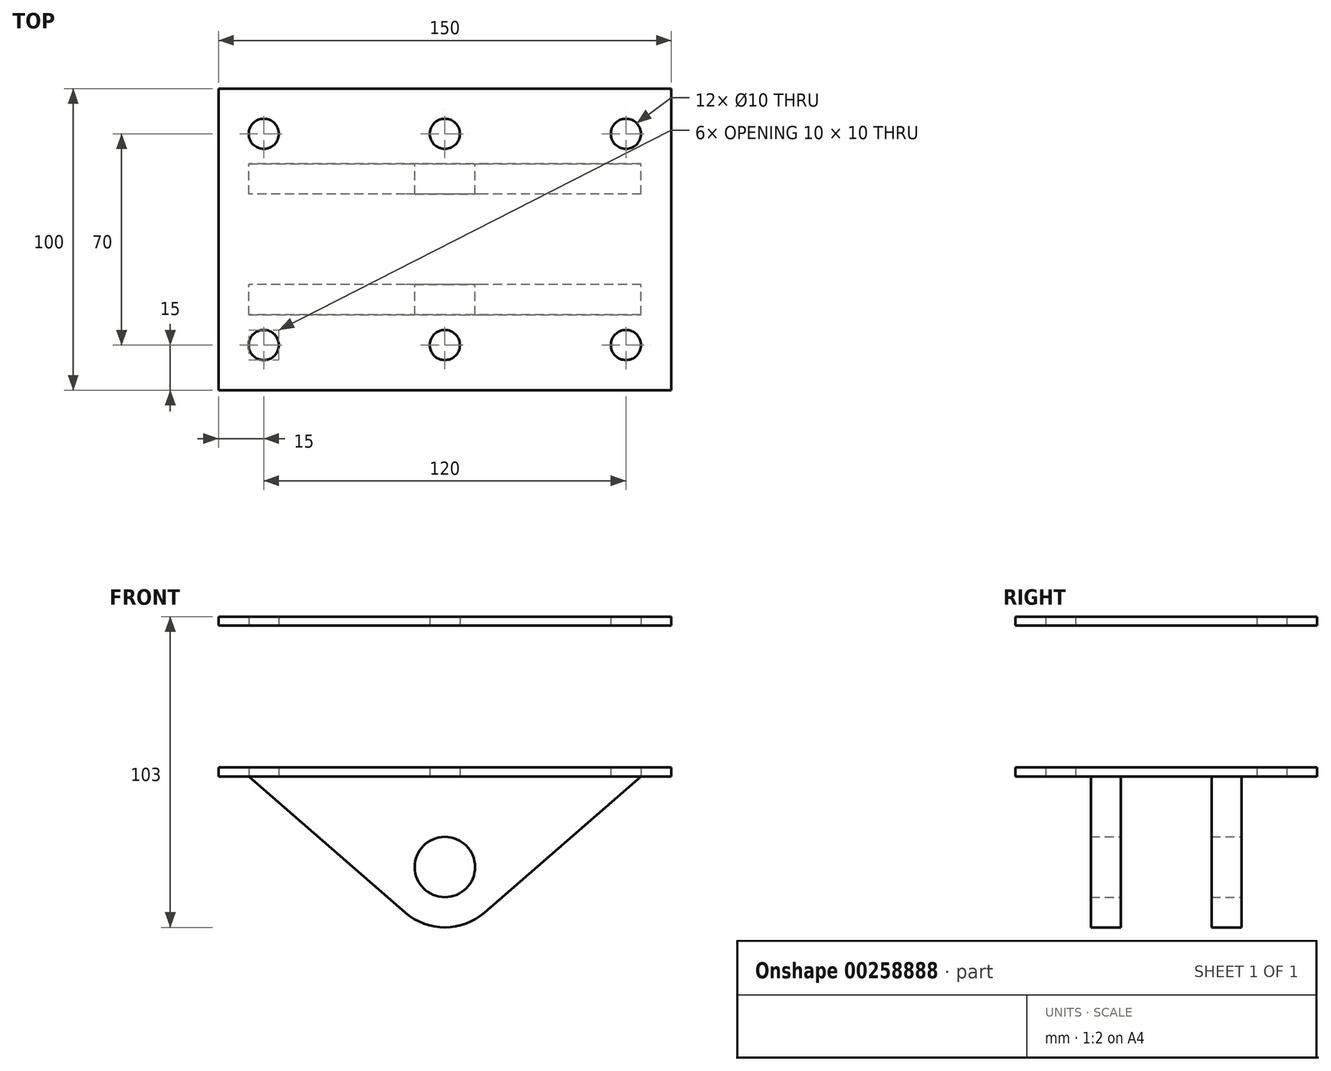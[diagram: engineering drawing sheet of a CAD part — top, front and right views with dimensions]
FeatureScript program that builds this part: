
annotation { "Feature Type Name" : "Feature", "Feature Type Description" : "" }
export const myFeature = defineFeature(function(context is Context, id is Id, definition is map)
    precondition{}
    {
        {
            var Q0;
            Q0=qCreatedBy(makeId("Top.planeOp"),FACE);
            var sketch = newSketch(context, id + "F0", { "sketchPlane" : qUnion([Q0])});
            skLineSegment(sketch, "E0.bottom", {"start": v(-75, 50) * mm, "end": v(75, 50) * mm});
            skLineSegment(sketch, "E0.top", {"start": v(-75, -50) * mm, "end": v(75, -50) * mm});
            skLineSegment(sketch, "E0.left", {"start": v(-75, 50) * mm, "end": v(-75, -50) * mm});
            skLineSegment(sketch, "E0.right", {"start": v(75, 50) * mm, "end": v(75, -50) * mm});
            skPoint(sketch, "E0.middle", {"position": v(0, 0) * mm});
            skLineSegment(sketch, "E1.bottom", {"start": v(-60, 35) * mm, "end": v(60, 35) * mm, "construction": true});
            skLineSegment(sketch, "E1.top", {"start": v(-60, -35) * mm, "end": v(60, -35) * mm, "construction": true});
            skLineSegment(sketch, "E1.left", {"start": v(-60, 35) * mm, "end": v(-60, -35) * mm, "construction": true});
            skLineSegment(sketch, "E1.right", {"start": v(60, 35) * mm, "end": v(60, -35) * mm, "construction": true});
            skCircle(sketch, "E2", {"center": v(-60, 35) * mm, "radius": 5 * mm});
            skCircle(sketch, "E3", {"center": v(-60, -35) * mm, "radius": 5 * mm});
            skCircle(sketch, "E4", {"center": v(60, -35) * mm, "radius": 5 * mm});
            skCircle(sketch, "E5", {"center": v(60, 35) * mm, "radius": 5 * mm});
            skCircle(sketch, "E6", {"center": v(0, 35) * mm, "radius": 5 * mm});
            skCircle(sketch, "E7", {"center": v(0, -35) * mm, "radius": 5 * mm});
            skSolve(sketch);
        }
        {
            var Q0;
            Q0=qCreatedBy(makeId("Right.planeOp"),FACE);
            var sketch = newSketch(context, id + "F1", { "sketchPlane" : qUnion([Q0])});
            skLineSegment(sketch, "E8", {"start": v(-15, 0) * mm, "end": v(-15, -100) * mm});
            skLineSegment(sketch, "E9", {"start": v(-15, -100) * mm, "end": v(-25, -100) * mm});
            skLineSegment(sketch, "E10", {"start": v(-25, -100) * mm, "end": v(-25, 0) * mm});
            skLineSegment(sketch, "E11", {"start": v(-25, 0) * mm, "end": v(-15, 0) * mm, "construction": true});
            skLineSegment(sketch, "E12.MirrorCS", {"start": v(15, 0) * mm, "end": v(15, -100) * mm});
            skLineSegment(sketch, "E13.MirrorCS", {"start": v(25, -100) * mm, "end": v(25, 0) * mm});
            skLineSegment(sketch, "E14.MirrorCS", {"start": v(25, 0) * mm, "end": v(15, 0) * mm, "construction": true});
            skLineSegment(sketch, "E15.MirrorCS", {"start": v(15, -100) * mm, "end": v(25, -100) * mm});
            skLineSegment(sketch, "E16", {"start": v(15, 0) * mm, "end": v(-15, 0) * mm});
            skLineSegment(sketch, "E17", {"start": v(-25, 0) * mm, "end": v(-55, 0) * mm});
            skLineSegment(sketch, "E18", {"start": v(-55, 0) * mm, "end": v(-55, 3) * mm});
            skLineSegment(sketch, "E19", {"start": v(-55, 3) * mm, "end": v(55, 3) * mm});
            skLineSegment(sketch, "E20", {"start": v(55, 3) * mm, "end": v(55, 0) * mm});
            skLineSegment(sketch, "E21", {"start": v(55, 0) * mm, "end": v(25, 0) * mm});
            skLineSegment(sketch, "E22", {"start": v(-55, 50) * mm, "end": v(55, 50) * mm});
            skLineSegment(sketch, "E23", {"start": v(55, 50) * mm, "end": v(55, 53) * mm});
            skLineSegment(sketch, "E24", {"start": v(55, 53) * mm, "end": v(-55, 53) * mm});
            skLineSegment(sketch, "E25", {"start": v(-55, 53) * mm, "end": v(-55, 50) * mm});
            skSolve(sketch);
        }
        {
            var Q0;
            Q0=qCreatedBy(makeId("Front.planeOp"),FACE);
            var sketch = newSketch(context, id + "F2", { "sketchPlane" : qUnion([Q0])});
            skCircle(sketch, "E26", {"center": v(0, -30) * mm, "radius": 10 * mm});
            skArc(sketch, "E27", {"start": v(20, -30) * mm, "mid": v(0, -50) * mm, "end": v(-20, -30) * mm});
            skLineSegment(sketch, "E28", {"start": v(-20, -30) * mm, "end": v(-20, 0) * mm, "construction": true});
            skLineSegment(sketch, "E29", {"start": v(-20, 0) * mm, "end": v(-65, 0) * mm});
            skLineSegment(sketch, "E30", {"start": v(20, -30) * mm, "end": v(20, 0) * mm, "construction": true});
            skLineSegment(sketch, "E31", {"start": v(20, 0) * mm, "end": v(65, 0) * mm});
            skLineSegment(sketch, "E32", {"start": v(-20, 0) * mm, "end": v(20, 0) * mm});
            skLineSegment(sketch, "E33", {"start": v(13.12, -45.1) * mm, "end": v(65, 0) * mm});
            skLineSegment(sketch, "E34", {"start": v(-65, 0) * mm, "end": v(-13.12, -45.1) * mm});
            skLineSegment(sketch, "E35", {"start": v(-65, 0) * mm, "end": v(-75, 0) * mm});
            skLineSegment(sketch, "E36", {"start": v(-75, 0) * mm, "end": v(-75, 3) * mm});
            skLineSegment(sketch, "E37", {"start": v(-75, 3) * mm, "end": v(75, 3) * mm});
            skLineSegment(sketch, "E38", {"start": v(75, 3) * mm, "end": v(75, 0) * mm});
            skLineSegment(sketch, "E39", {"start": v(75, 0) * mm, "end": v(65, 0) * mm});
            skLineSegment(sketch, "E40", {"start": v(-75, 50) * mm, "end": v(75, 50) * mm});
            skLineSegment(sketch, "E41", {"start": v(75, 50) * mm, "end": v(75, 53) * mm});
            skLineSegment(sketch, "E42", {"start": v(75, 53) * mm, "end": v(-75, 53) * mm});
            skLineSegment(sketch, "E43", {"start": v(-75, 53) * mm, "end": v(-75, 50) * mm});
            skSolve(sketch);
        }
        {
            var Q0;
            Q0 = qSketchRegion(id + "F0", true);
            extrude(context, id + "F3", {"entities" : qUnion([Q0]), "depth" : 448 * mm, "symmetric" : true});
        }
        {
            var Q0;
            Q0 = qSketchRegion(id + "F2", true);
            extrude(context, id + "F4", {"entities" : qUnion([Q0]), "operationType" : NewBodyOperationType.INTERSECT, "depth" : 100 * mm, "symmetric" : true});
        }
        {
            var Q0;
            Q0 = qSketchRegion(id + "F1", true);
            extrude(context, id + "F5", {"entities" : qUnion([Q0]), "operationType" : NewBodyOperationType.INTERSECT, "depth" : 1260 * mm, "symmetric" : true});
        }
    });
